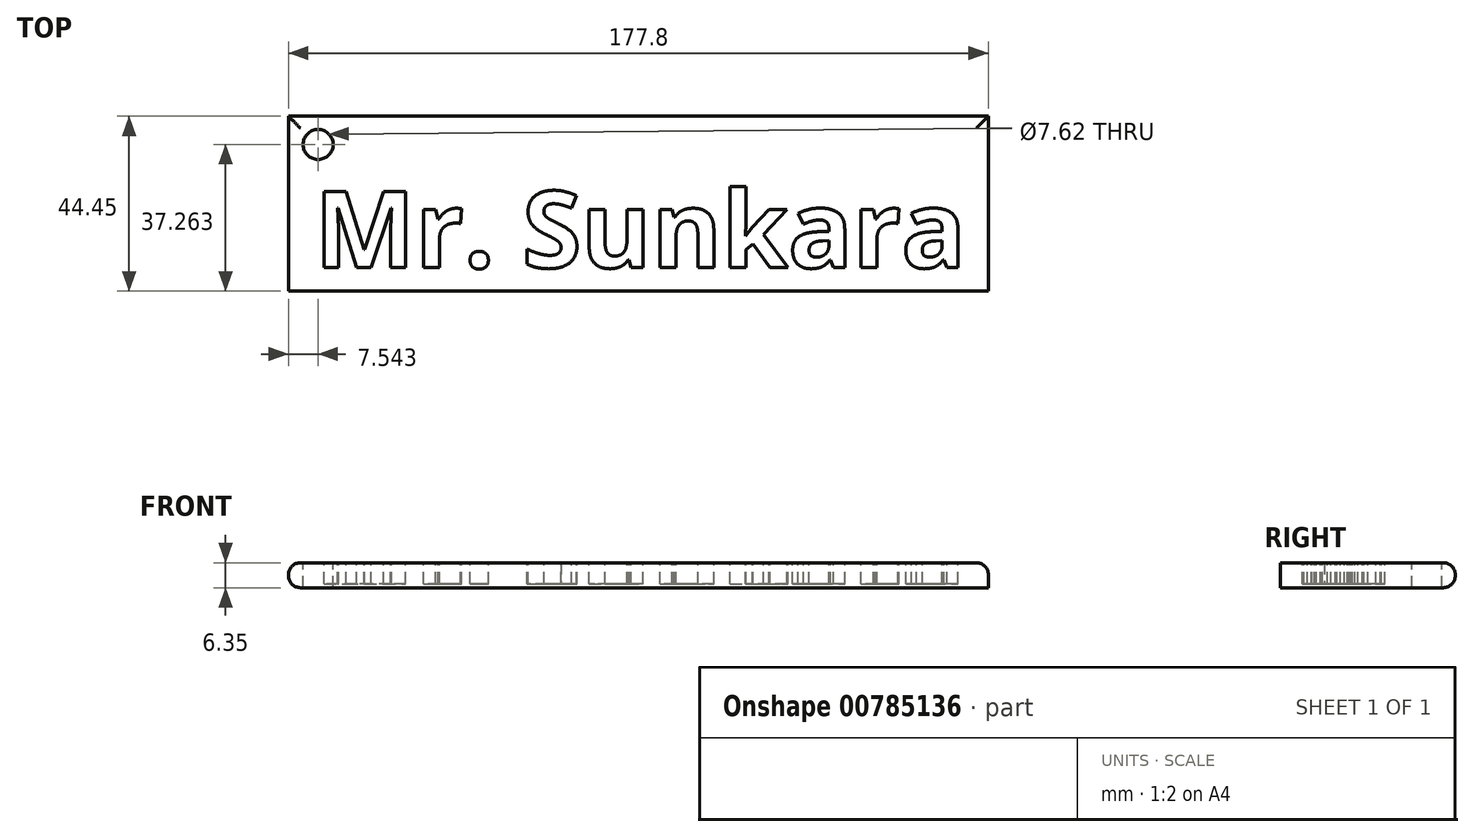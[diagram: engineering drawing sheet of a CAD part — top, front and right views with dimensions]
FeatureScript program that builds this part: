
annotation { "Feature Type Name" : "Feature", "Feature Type Description" : "" }
export const myFeature = defineFeature(function(context is Context, id is Id, definition is map)
    precondition{}
    {
        {
            var Q0;
            Q0=qCreatedBy(makeId("Top.planeOp"),FACE);
            var sketch = newSketch(context, id + "F0", { "sketchPlane" : qUnion([Q0])});
            skLineSegment(sketch, "E0.bottom", {"start": v(-63.09, 49.5) * mm, "end": v(114.71, 49.5) * mm});
            skLineSegment(sketch, "E0.top", {"start": v(-63.09, 5.05) * mm, "end": v(114.71, 5.05) * mm});
            skLineSegment(sketch, "E0.left", {"start": v(-63.09, 49.5) * mm, "end": v(-63.09, 5.05) * mm});
            skLineSegment(sketch, "E0.right", {"start": v(114.71, 49.5) * mm, "end": v(114.71, 5.05) * mm});
            skSolve(sketch);
        }
        {
            var Q0;
            Q0=makeQuery(id+"F0.imprint","IMPRINT",FACE,{"disambiguationData":[TD([[makeQuery(id+"F0.imprint","IMPRINT",EDGE,{"derivedFrom":sQuery(id+"F0.wireOp",EDGE,"E0.bottom")}),-1.0]])]});
            extrude(context, id + "F1", {"entities" : qUnion([Q0]), "depth" : 6.35 * mm, "offsetDistance" : 25.4 * mm});
        }
        {
            var Q0;
            Q0=makeQuery(id+"F1.opExtrude","CAP_FACE",FACE,{"disambiguationData":[OSD([sQuery(id+"F0.wireOp",EDGE,"E0.bottom"),sQuery(id+"F0.wireOp",EDGE,"E0.top"),sQuery(id+"F0.wireOp",EDGE,"E0.left"),sQuery(id+"F0.wireOp",EDGE,"E0.right")])],"isStart":false});
            var sketch = newSketch(context, id + "F2", { "sketchPlane" : qUnion([Q0])});
            skCircle(sketch, "E1", {"center": v(-55.55, 42.31) * mm, "radius": 3.81 * mm});
            skSolve(sketch);
        }
        {
            var Q0;
            Q0=makeQuery(id+"F2.imprint","IMPRINT",FACE,{"disambiguationData":[TD([[makeQuery(id+"F2.imprint","IMPRINT",EDGE,{"derivedFrom":sQuery(id+"F2.wireOp",EDGE,"E1")}),1.0]])]});
            extrude(context, id + "F3", {"entities" : qUnion([Q0]), "operationType" : NewBodyOperationType.REMOVE, "oppositeDirection" : true, "depth" : 70.87 * mm, "offsetDistance" : 25.4 * mm});
        }
        {
            var Q0;
            Q0=makeQuery(id+"F1.opExtrude","CAP_FACE",FACE,{"disambiguationData":[OSD([sQuery(id+"F0.wireOp",EDGE,"E0.bottom"),sQuery(id+"F0.wireOp",EDGE,"E0.top"),sQuery(id+"F0.wireOp",EDGE,"E0.left"),sQuery(id+"F0.wireOp",EDGE,"E0.right")])],"isStart":false});
            var sketch = newSketch(context, id + "F4", { "sketchPlane" : qUnion([Q0])});
            skText(sketch, "E2", { "text": "Mr. Sunkara", "fontName": "OpenSans-Bold.ttf"});
            const initialGuessF4  = {"E2": [-0.05647, 0.011, 1, 0, 0.01957]};
            skSetInitialGuess(sketch, initialGuessF4);
            skSolve(sketch);
        }
        {
            var Q0;
            Q0 = qSketchRegion(id + "F4", true);
            extrude(context, id + "F5", {"entities" : qUnion([Q0]), "operationType" : NewBodyOperationType.REMOVE, "oppositeDirection" : true, "depth" : 5.33 * mm, "offsetDistance" : 25.4 * mm});
        }
        {
            var Q0;
            Q0=makeQuery(id+"F1.opExtrude","CAP_EDGE",EDGE,{"disambiguationData":[OSD([sQuery(id+"F0.wireOp",EDGE,"E0.bottom")])],"isStart":false});
            var Q1;
            Q1=makeQuery(id+"F1.opExtrude","CAP_EDGE",EDGE,{"disambiguationData":[OSD([sQuery(id+"F0.wireOp",EDGE,"E0.bottom")])],"isStart":true});
            var Q2;
            Q2=makeQuery(id+"F1.opExtrude","CAP_EDGE",EDGE,{"disambiguationData":[OSD([sQuery(id+"F0.wireOp",EDGE,"E0.left")])],"isStart":false});
            var Q3;
            Q3=makeQuery(id+"F1.opExtrude","CAP_EDGE",EDGE,{"disambiguationData":[OSD([sQuery(id+"F0.wireOp",EDGE,"E0.left")])],"isStart":true});
            var Q4;
            Q4=makeQuery(id+"F1.opExtrude","CAP_EDGE",EDGE,{"disambiguationData":[OSD([sQuery(id+"F0.wireOp",EDGE,"E0.right")])],"isStart":false});
            fillet(context, id + "F6", {"entities" : qUnion([Q0, Q1, Q2, Q3, Q4]), "radius" : 3.05 * mm, "tangentPropagation" : true, "allowEdgeOverflow" : false});
        }
    });
